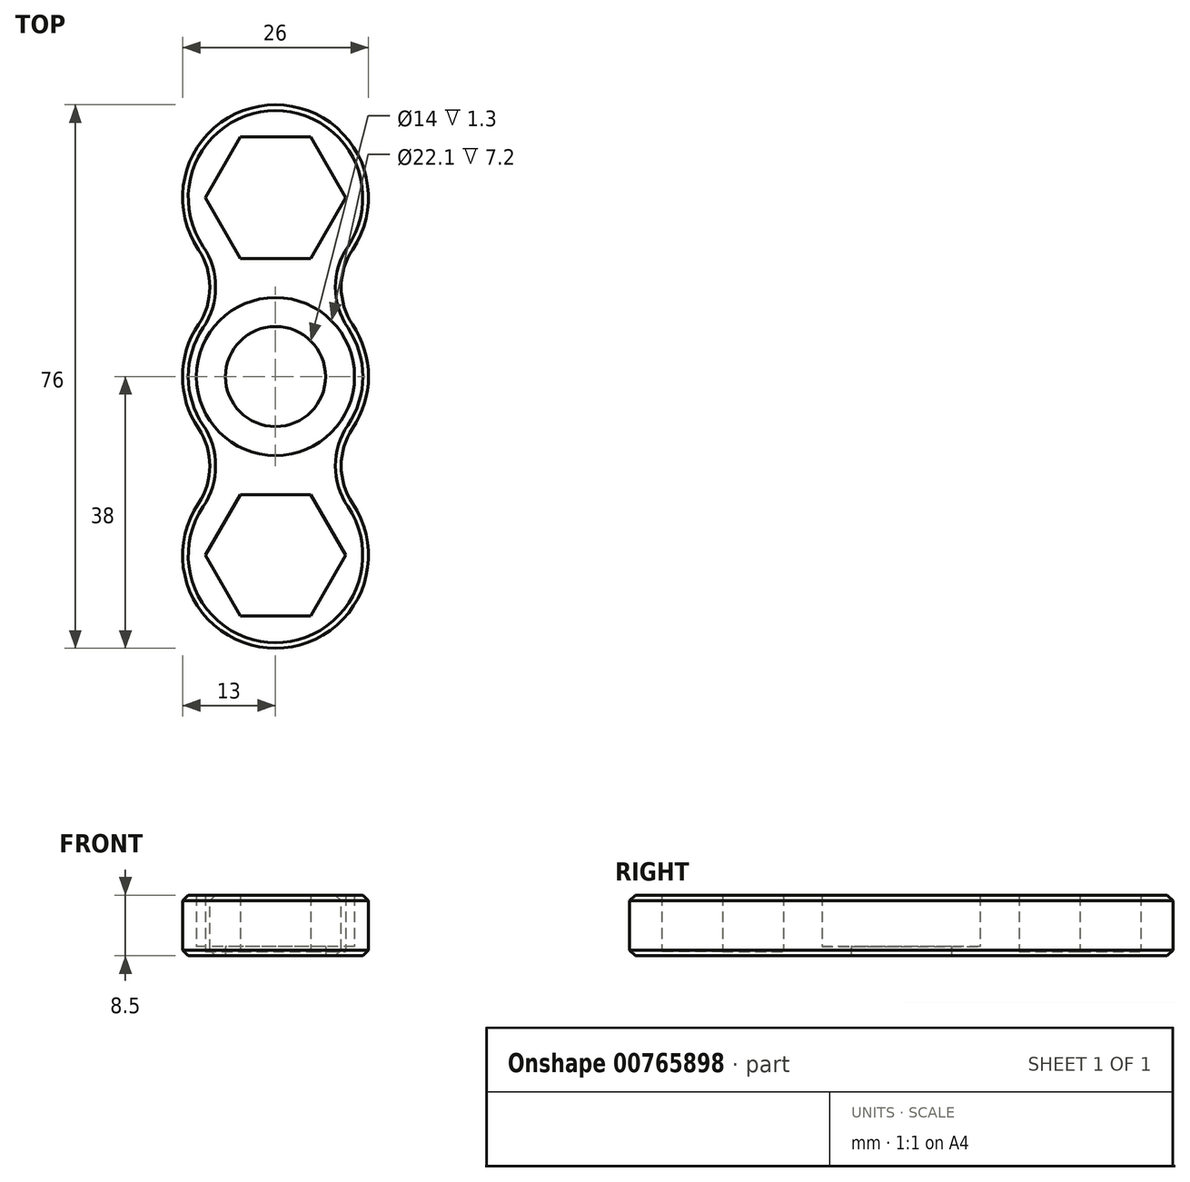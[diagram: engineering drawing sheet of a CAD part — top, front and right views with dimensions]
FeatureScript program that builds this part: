
annotation { "Feature Type Name" : "Feature", "Feature Type Description" : "" }
export const myFeature = defineFeature(function(context is Context, id is Id, definition is map)
    precondition{}
    {
        {
            var Q0;
            Q0=qCreatedBy(makeId("Top.planeOp"),FACE);
            var sketch = newSketch(context, id + "F0", { "sketchPlane" : qUnion([Q0])});
            skCircle(sketch, "E0", {"center": v(0, 0) * mm, "radius": 13 * mm});
            skCircle(sketch, "E1", {"center": v(0, 0) * mm, "radius": 11.05 * mm});
            skCircle(sketch, "E2", {"center": v(0, 25) * mm, "radius": 13 * mm});
            skCircle(sketch, "E3.cCircle", {"center": v(0, 25) * mm, "radius": 8.5 * mm, "construction": true});
            skLineSegment(sketch, "E3.0", {"start": v(9.81, 25) * mm, "end": v(4.9, 16.5) * mm});
            skLineSegment(sketch, "E3.1", {"start": v(4.9, 16.5) * mm, "end": v(-4.9, 16.5) * mm});
            skLineSegment(sketch, "E3.2", {"start": v(-4.9, 16.5) * mm, "end": v(-9.81, 25) * mm});
            skLineSegment(sketch, "E3.3", {"start": v(-9.81, 25) * mm, "end": v(-4.9, 33.5) * mm});
            skLineSegment(sketch, "E3.4", {"start": v(-4.9, 33.5) * mm, "end": v(4.9, 33.5) * mm});
            skLineSegment(sketch, "E3.5", {"start": v(4.9, 33.5) * mm, "end": v(9.81, 25) * mm});
            skPoint(sketch, "E3.0.midPoint", {"position": v(7.36, 20.75) * mm});
            skCircle(sketch, "E4.MirrorC", {"center": v(0, -25) * mm, "radius": 13 * mm});
            skLineSegment(sketch, "E5.MirrorCS", {"start": v(-4.9, -16.5) * mm, "end": v(-9.81, -25) * mm});
            skCircle(sketch, "E6.MirrorC", {"center": v(0, -25) * mm, "radius": 8.5 * mm, "construction": true});
            skLineSegment(sketch, "E7.MirrorCS", {"start": v(-9.81, -25) * mm, "end": v(-4.9, -33.5) * mm});
            skLineSegment(sketch, "E8.MirrorCS", {"start": v(-4.9, -33.5) * mm, "end": v(4.9, -33.5) * mm});
            skLineSegment(sketch, "E9.MirrorCS", {"start": v(4.9, -33.5) * mm, "end": v(9.81, -25) * mm});
            skLineSegment(sketch, "E10.MirrorCS", {"start": v(9.81, -25) * mm, "end": v(4.9, -16.5) * mm});
            skLineSegment(sketch, "E11.MirrorCS", {"start": v(4.9, -16.5) * mm, "end": v(-4.9, -16.5) * mm});
            skCircle(sketch, "E12", {"center": v(0, 0) * mm, "radius": 7 * mm});
            skSolve(sketch);
        }
        {
            var Q0;
            Q0=makeQuery(id+"F0.imprint","IMPRINT",FACE,{"disambiguationData":[TD([[makeQuery(id+"F0.imprint","IMPRINT",EDGE,{"derivedFrom":sQuery(id+"F0.wireOp",EDGE,"E3.0")}),1.0]])]});
            var Q1;
            Q1=makeQuery(id+"F0.imprint","IMPRINT",FACE,{"disambiguationData":[TD([[makeQuery(id+"F0.imprint","IMPRINT",EDGE,{"derivedFrom":sQuery(id+"F0.wireOp",EDGE,"E3.0")}),-1.0]])]});
            var Q2;
            Q2=makeQuery(id+"F0.imprint","IMPRINT",FACE,{"disambiguationData":[TD([[makeQuery(id+"F0.imprint","IMPRINT",EDGE,{"derivedFrom":sQuery(id+"F0.wireOp",EDGE,"E1")}),1.0]])]});
            var Q3;
            Q3=makeQuery(id+"F0.imprint","IMPRINT",FACE,{"disambiguationData":[TD([[makeQuery(id+"F0.imprint","IMPRINT",EDGE,{"derivedFrom":sQuery(id+"F0.wireOp",EDGE,"E1")}),-1.0]])]});
            var Q4;
            {var subQ0=sQuery(id+"F0.wireOp",EDGE,"E2");var subQ1=sQuery(id+"F0.wireOp",EDGE,"E0");var subQ2=makeQuery(id+"F0.imprint","INTERSECT",VERTEX,{"disambiguationData":[OD(0.0)],"derivedFrom":[subQ1,subQ0]});Q4=makeQuery(id+"F0.imprint","IMPRINT",FACE,{"disambiguationData":[TD([[makeQuery(id+"F0.imprint","IMPRINT",EDGE,{"disambiguationData":[TD([[subQ2,1.0]])],"derivedFrom":subQ1}),1.0]])]});}
            var Q5;
            {var subQ0=sQuery(id+"F0.wireOp",EDGE,"E4.MirrorC");var subQ1=sQuery(id+"F0.wireOp",EDGE,"E0");var subQ2=makeQuery(id+"F0.imprint","INTERSECT",VERTEX,{"disambiguationData":[OD(0.0)],"derivedFrom":[subQ1,subQ0]});Q5=makeQuery(id+"F0.imprint","IMPRINT",FACE,{"disambiguationData":[TD([[makeQuery(id+"F0.imprint","IMPRINT",EDGE,{"disambiguationData":[TD([[subQ2,-1.0]])],"derivedFrom":subQ1}),1.0]])]});}
            var Q6;
            Q6=makeQuery(id+"F0.imprint","IMPRINT",FACE,{"disambiguationData":[TD([[makeQuery(id+"F0.imprint","IMPRINT",EDGE,{"derivedFrom":sQuery(id+"F0.wireOp",EDGE,"E5.MirrorCS")}),-1.0]])]});
            var Q7;
            Q7=makeQuery(id+"F0.imprint","IMPRINT",FACE,{"disambiguationData":[TD([[makeQuery(id+"F0.imprint","IMPRINT",EDGE,{"derivedFrom":sQuery(id+"F0.wireOp",EDGE,"E5.MirrorCS")}),1.0]])]});
            extrude(context, id + "F1", {"entities" : qUnion([Q0, Q1, Q2, Q3, Q4, Q5, Q6, Q7]), "depth" : 0.6 * mm, "offsetDistance" : 25 * mm});
        }
        {
            var Q0;
            Q0=makeQuery(id+"F0.imprint","IMPRINT",FACE,{"disambiguationData":[TD([[makeQuery(id+"F0.imprint","IMPRINT",EDGE,{"derivedFrom":sQuery(id+"F0.wireOp",EDGE,"E3.0")}),1.0]])]});
            var Q1;
            Q1=makeQuery(id+"F0.imprint","IMPRINT",FACE,{"disambiguationData":[TD([[makeQuery(id+"F0.imprint","IMPRINT",EDGE,{"derivedFrom":sQuery(id+"F0.wireOp",EDGE,"E1")}),-1.0]])]});
            var Q2;
            {var subQ0=sQuery(id+"F0.wireOp",EDGE,"E2");var subQ1=sQuery(id+"F0.wireOp",EDGE,"E0");var subQ2=makeQuery(id+"F0.imprint","INTERSECT",VERTEX,{"disambiguationData":[OD(0.0)],"derivedFrom":[subQ1,subQ0]});Q2=makeQuery(id+"F0.imprint","IMPRINT",FACE,{"disambiguationData":[TD([[makeQuery(id+"F0.imprint","IMPRINT",EDGE,{"disambiguationData":[TD([[subQ2,1.0]])],"derivedFrom":subQ1}),1.0]])]});}
            var Q3;
            {var subQ0=sQuery(id+"F0.wireOp",EDGE,"E4.MirrorC");var subQ1=sQuery(id+"F0.wireOp",EDGE,"E0");var subQ2=makeQuery(id+"F0.imprint","INTERSECT",VERTEX,{"disambiguationData":[OD(0.0)],"derivedFrom":[subQ1,subQ0]});Q3=makeQuery(id+"F0.imprint","IMPRINT",FACE,{"disambiguationData":[TD([[makeQuery(id+"F0.imprint","IMPRINT",EDGE,{"disambiguationData":[TD([[subQ2,-1.0]])],"derivedFrom":subQ1}),1.0]])]});}
            var Q4;
            Q4=makeQuery(id+"F0.imprint","IMPRINT",FACE,{"disambiguationData":[TD([[makeQuery(id+"F0.imprint","IMPRINT",EDGE,{"derivedFrom":sQuery(id+"F0.wireOp",EDGE,"E5.MirrorCS")}),-1.0]])]});
            extrude(context, id + "F2", {"entities" : qUnion([Q0, Q1, Q2, Q3, Q4]), "operationType" : NewBodyOperationType.ADD, "depth" : 8.5 * mm, "offsetDistance" : 25 * mm});
        }
        {
            var Q0;
            {var subQ0=sQuery(id+"F0.wireOp",EDGE,"E4.MirrorC");var subQ1=sQuery(id+"F0.wireOp",EDGE,"E0");var subQ2=makeQuery(id+"F0.imprint","INTERSECT",VERTEX,{"disambiguationData":[OD(1.0)],"derivedFrom":[subQ1,subQ0]});Q0=makeQuery(id+"F2.boolean.opBoolean","MERGE",EDGE,{"derivedFrom":[makeQuery(id+"F1.opExtrude","SWEPT_EDGE",EDGE,{"disambiguationData":[OSD([subQ1,subQ0]),TDD([subQ2])]}),makeQuery(id+"F2.opExtrude","SWEPT_EDGE",EDGE,{"disambiguationData":[OSD([subQ1,subQ0]),TDD([subQ2])]})]});}
            var Q1;
            {var subQ0=sQuery(id+"F0.wireOp",EDGE,"E2");var subQ1=sQuery(id+"F0.wireOp",EDGE,"E0");var subQ2=makeQuery(id+"F0.imprint","INTERSECT",VERTEX,{"disambiguationData":[OD(1.0)],"derivedFrom":[subQ1,subQ0]});Q1=makeQuery(id+"F2.boolean.opBoolean","MERGE",EDGE,{"derivedFrom":[makeQuery(id+"F1.opExtrude","SWEPT_EDGE",EDGE,{"disambiguationData":[OSD([subQ1,subQ0]),TDD([subQ2])]}),makeQuery(id+"F2.opExtrude","SWEPT_EDGE",EDGE,{"disambiguationData":[OSD([subQ1,subQ0]),TDD([subQ2])]})]});}
            var Q2;
            {var subQ0=sQuery(id+"F0.wireOp",EDGE,"E2");var subQ1=sQuery(id+"F0.wireOp",EDGE,"E0");var subQ2=makeQuery(id+"F0.imprint","INTERSECT",VERTEX,{"disambiguationData":[OD(0.0)],"derivedFrom":[subQ1,subQ0]});Q2=makeQuery(id+"F2.boolean.opBoolean","MERGE",EDGE,{"derivedFrom":[makeQuery(id+"F1.opExtrude","SWEPT_EDGE",EDGE,{"disambiguationData":[OSD([subQ1,subQ0]),TDD([subQ2])]}),makeQuery(id+"F2.opExtrude","SWEPT_EDGE",EDGE,{"disambiguationData":[OSD([subQ1,subQ0]),TDD([subQ2])]})]});}
            var Q3;
            {var subQ0=sQuery(id+"F0.wireOp",EDGE,"E4.MirrorC");var subQ1=sQuery(id+"F0.wireOp",EDGE,"E0");var subQ2=makeQuery(id+"F0.imprint","INTERSECT",VERTEX,{"disambiguationData":[OD(0.0)],"derivedFrom":[subQ1,subQ0]});Q3=makeQuery(id+"F2.boolean.opBoolean","MERGE",EDGE,{"derivedFrom":[makeQuery(id+"F1.opExtrude","SWEPT_EDGE",EDGE,{"disambiguationData":[OSD([subQ1,subQ0]),TDD([subQ2])]}),makeQuery(id+"F2.opExtrude","SWEPT_EDGE",EDGE,{"disambiguationData":[OSD([subQ1,subQ0]),TDD([subQ2])]})]});}
            fillet(context, id + "F3", {"entities" : qUnion([Q0, Q1, Q2, Q3]), "radius" : 9.35 * mm, "tangentPropagation" : true, "allowEdgeOverflow" : false});
        }
        {
            var Q0;
            Q0=makeQuery(id+"F2.opExtrude","CAP_EDGE",EDGE,{"disambiguationData":[OSD([sQuery(id+"F0.wireOp",EDGE,"E4.MirrorC")])],"isStart":false});
            var Q1;
            {var subQ0=sQuery(id+"F0.wireOp",EDGE,"E4.MirrorC");var subQ1=sQuery(id+"F0.wireOp",EDGE,"E0");var subQ2=makeQuery(id+"F0.imprint","INTERSECT",VERTEX,{"disambiguationData":[OD(1.0)],"derivedFrom":[subQ1,subQ0]});Q1=makeQuery(id+"F3.opFillet","BLEND_EDGE",EDGE,{"blendedFrom":[makeQuery(id+"F2.boolean.opBoolean","MERGE",EDGE,{"derivedFrom":[makeQuery(id+"F1.opExtrude","SWEPT_EDGE",EDGE,{"disambiguationData":[OSD([subQ1,subQ0]),TDD([subQ2])]}),makeQuery(id+"F2.opExtrude","SWEPT_EDGE",EDGE,{"disambiguationData":[OSD([subQ1,subQ0]),TDD([subQ2])]})]}),makeQuery(id+"F2.opExtrude","CAP_FACE",FACE,{"disambiguationData":[OSD([subQ1,sQuery(id+"F0.wireOp",EDGE,"E1"),sQuery(id+"F0.wireOp",EDGE,"E2"),sQuery(id+"F0.wireOp",EDGE,"E3.0"),sQuery(id+"F0.wireOp",EDGE,"E3.1"),sQuery(id+"F0.wireOp",EDGE,"E3.2"),sQuery(id+"F0.wireOp",EDGE,"E3.3"),sQuery(id+"F0.wireOp",EDGE,"E3.4"),sQuery(id+"F0.wireOp",EDGE,"E3.5"),subQ0,sQuery(id+"F0.wireOp",EDGE,"E5.MirrorCS"),sQuery(id+"F0.wireOp",EDGE,"E7.MirrorCS"),sQuery(id+"F0.wireOp",EDGE,"E8.MirrorCS"),sQuery(id+"F0.wireOp",EDGE,"E9.MirrorCS"),sQuery(id+"F0.wireOp",EDGE,"E10.MirrorCS"),sQuery(id+"F0.wireOp",EDGE,"E11.MirrorCS")])],"isStart":false})],"blendedInto":[makeQuery(id+"F2.opExtrude","CAP_FACE",FACE,{"disambiguationData":[OSD([subQ1,sQuery(id+"F0.wireOp",EDGE,"E1"),sQuery(id+"F0.wireOp",EDGE,"E2"),sQuery(id+"F0.wireOp",EDGE,"E3.0"),sQuery(id+"F0.wireOp",EDGE,"E3.1"),sQuery(id+"F0.wireOp",EDGE,"E3.2"),sQuery(id+"F0.wireOp",EDGE,"E3.3"),sQuery(id+"F0.wireOp",EDGE,"E3.4"),sQuery(id+"F0.wireOp",EDGE,"E3.5"),subQ0,sQuery(id+"F0.wireOp",EDGE,"E5.MirrorCS"),sQuery(id+"F0.wireOp",EDGE,"E7.MirrorCS"),sQuery(id+"F0.wireOp",EDGE,"E8.MirrorCS"),sQuery(id+"F0.wireOp",EDGE,"E9.MirrorCS"),sQuery(id+"F0.wireOp",EDGE,"E10.MirrorCS"),sQuery(id+"F0.wireOp",EDGE,"E11.MirrorCS")])],"isStart":false})]});}
            var Q2;
            {var subQ0=sQuery(id+"F0.wireOp",EDGE,"E0");Q2=makeQuery(id+"F2.opExtrude","CAP_EDGE",EDGE,{"disambiguationData":[OSD([subQ0]),TDD([makeQuery(id+"F0.imprint","IMPRINT",EDGE,{"disambiguationData":[TD([[makeQuery(id+"F0.imprint","INTERSECT",VERTEX,{"disambiguationData":[OD(1.0)],"derivedFrom":[subQ0,sQuery(id+"F0.wireOp",EDGE,"E2")]}),1.0]])],"derivedFrom":subQ0})])],"isStart":false});}
            var Q3;
            {var subQ0=sQuery(id+"F0.wireOp",EDGE,"E2");var subQ1=sQuery(id+"F0.wireOp",EDGE,"E0");var subQ2=makeQuery(id+"F0.imprint","INTERSECT",VERTEX,{"disambiguationData":[OD(1.0)],"derivedFrom":[subQ1,subQ0]});Q3=makeQuery(id+"F3.opFillet","BLEND_EDGE",EDGE,{"blendedFrom":[makeQuery(id+"F2.boolean.opBoolean","MERGE",EDGE,{"derivedFrom":[makeQuery(id+"F1.opExtrude","SWEPT_EDGE",EDGE,{"disambiguationData":[OSD([subQ1,subQ0]),TDD([subQ2])]}),makeQuery(id+"F2.opExtrude","SWEPT_EDGE",EDGE,{"disambiguationData":[OSD([subQ1,subQ0]),TDD([subQ2])]})]}),makeQuery(id+"F2.opExtrude","CAP_FACE",FACE,{"disambiguationData":[OSD([subQ1,sQuery(id+"F0.wireOp",EDGE,"E1"),subQ0,sQuery(id+"F0.wireOp",EDGE,"E3.0"),sQuery(id+"F0.wireOp",EDGE,"E3.1"),sQuery(id+"F0.wireOp",EDGE,"E3.2"),sQuery(id+"F0.wireOp",EDGE,"E3.3"),sQuery(id+"F0.wireOp",EDGE,"E3.4"),sQuery(id+"F0.wireOp",EDGE,"E3.5"),sQuery(id+"F0.wireOp",EDGE,"E4.MirrorC"),sQuery(id+"F0.wireOp",EDGE,"E5.MirrorCS"),sQuery(id+"F0.wireOp",EDGE,"E7.MirrorCS"),sQuery(id+"F0.wireOp",EDGE,"E8.MirrorCS"),sQuery(id+"F0.wireOp",EDGE,"E9.MirrorCS"),sQuery(id+"F0.wireOp",EDGE,"E10.MirrorCS"),sQuery(id+"F0.wireOp",EDGE,"E11.MirrorCS")])],"isStart":false})],"blendedInto":[makeQuery(id+"F2.opExtrude","CAP_FACE",FACE,{"disambiguationData":[OSD([subQ1,sQuery(id+"F0.wireOp",EDGE,"E1"),subQ0,sQuery(id+"F0.wireOp",EDGE,"E3.0"),sQuery(id+"F0.wireOp",EDGE,"E3.1"),sQuery(id+"F0.wireOp",EDGE,"E3.2"),sQuery(id+"F0.wireOp",EDGE,"E3.3"),sQuery(id+"F0.wireOp",EDGE,"E3.4"),sQuery(id+"F0.wireOp",EDGE,"E3.5"),sQuery(id+"F0.wireOp",EDGE,"E4.MirrorC"),sQuery(id+"F0.wireOp",EDGE,"E5.MirrorCS"),sQuery(id+"F0.wireOp",EDGE,"E7.MirrorCS"),sQuery(id+"F0.wireOp",EDGE,"E8.MirrorCS"),sQuery(id+"F0.wireOp",EDGE,"E9.MirrorCS"),sQuery(id+"F0.wireOp",EDGE,"E10.MirrorCS"),sQuery(id+"F0.wireOp",EDGE,"E11.MirrorCS")])],"isStart":false})]});}
            var Q4;
            Q4=makeQuery(id+"F2.opExtrude","CAP_EDGE",EDGE,{"disambiguationData":[OSD([sQuery(id+"F0.wireOp",EDGE,"E2")])],"isStart":false});
            var Q5;
            {var subQ0=sQuery(id+"F0.wireOp",EDGE,"E2");var subQ1=sQuery(id+"F0.wireOp",EDGE,"E0");var subQ2=makeQuery(id+"F0.imprint","INTERSECT",VERTEX,{"disambiguationData":[OD(0.0)],"derivedFrom":[subQ1,subQ0]});Q5=makeQuery(id+"F3.opFillet","BLEND_EDGE",EDGE,{"blendedFrom":[makeQuery(id+"F2.boolean.opBoolean","MERGE",EDGE,{"derivedFrom":[makeQuery(id+"F1.opExtrude","SWEPT_EDGE",EDGE,{"disambiguationData":[OSD([subQ1,subQ0]),TDD([subQ2])]}),makeQuery(id+"F2.opExtrude","SWEPT_EDGE",EDGE,{"disambiguationData":[OSD([subQ1,subQ0]),TDD([subQ2])]})]}),makeQuery(id+"F2.opExtrude","CAP_FACE",FACE,{"disambiguationData":[OSD([subQ1,sQuery(id+"F0.wireOp",EDGE,"E1"),subQ0,sQuery(id+"F0.wireOp",EDGE,"E3.0"),sQuery(id+"F0.wireOp",EDGE,"E3.1"),sQuery(id+"F0.wireOp",EDGE,"E3.2"),sQuery(id+"F0.wireOp",EDGE,"E3.3"),sQuery(id+"F0.wireOp",EDGE,"E3.4"),sQuery(id+"F0.wireOp",EDGE,"E3.5"),sQuery(id+"F0.wireOp",EDGE,"E4.MirrorC"),sQuery(id+"F0.wireOp",EDGE,"E5.MirrorCS"),sQuery(id+"F0.wireOp",EDGE,"E7.MirrorCS"),sQuery(id+"F0.wireOp",EDGE,"E8.MirrorCS"),sQuery(id+"F0.wireOp",EDGE,"E9.MirrorCS"),sQuery(id+"F0.wireOp",EDGE,"E10.MirrorCS"),sQuery(id+"F0.wireOp",EDGE,"E11.MirrorCS")])],"isStart":false})],"blendedInto":[makeQuery(id+"F2.opExtrude","CAP_FACE",FACE,{"disambiguationData":[OSD([subQ1,sQuery(id+"F0.wireOp",EDGE,"E1"),subQ0,sQuery(id+"F0.wireOp",EDGE,"E3.0"),sQuery(id+"F0.wireOp",EDGE,"E3.1"),sQuery(id+"F0.wireOp",EDGE,"E3.2"),sQuery(id+"F0.wireOp",EDGE,"E3.3"),sQuery(id+"F0.wireOp",EDGE,"E3.4"),sQuery(id+"F0.wireOp",EDGE,"E3.5"),sQuery(id+"F0.wireOp",EDGE,"E4.MirrorC"),sQuery(id+"F0.wireOp",EDGE,"E5.MirrorCS"),sQuery(id+"F0.wireOp",EDGE,"E7.MirrorCS"),sQuery(id+"F0.wireOp",EDGE,"E8.MirrorCS"),sQuery(id+"F0.wireOp",EDGE,"E9.MirrorCS"),sQuery(id+"F0.wireOp",EDGE,"E10.MirrorCS"),sQuery(id+"F0.wireOp",EDGE,"E11.MirrorCS")])],"isStart":false})]});}
            var Q6;
            {var subQ0=sQuery(id+"F0.wireOp",EDGE,"E0");Q6=makeQuery(id+"F2.opExtrude","CAP_EDGE",EDGE,{"disambiguationData":[OSD([subQ0]),TDD([makeQuery(id+"F0.imprint","IMPRINT",EDGE,{"disambiguationData":[TD([[makeQuery(id+"F0.imprint","INTERSECT",VERTEX,{"disambiguationData":[OD(0.0)],"derivedFrom":[subQ0,sQuery(id+"F0.wireOp",EDGE,"E2")]}),-1.0]])],"derivedFrom":subQ0})])],"isStart":false});}
            var Q7;
            {var subQ0=sQuery(id+"F0.wireOp",EDGE,"E4.MirrorC");var subQ1=sQuery(id+"F0.wireOp",EDGE,"E0");var subQ2=makeQuery(id+"F0.imprint","INTERSECT",VERTEX,{"disambiguationData":[OD(0.0)],"derivedFrom":[subQ1,subQ0]});Q7=makeQuery(id+"F3.opFillet","BLEND_EDGE",EDGE,{"blendedFrom":[makeQuery(id+"F2.boolean.opBoolean","MERGE",EDGE,{"derivedFrom":[makeQuery(id+"F1.opExtrude","SWEPT_EDGE",EDGE,{"disambiguationData":[OSD([subQ1,subQ0]),TDD([subQ2])]}),makeQuery(id+"F2.opExtrude","SWEPT_EDGE",EDGE,{"disambiguationData":[OSD([subQ1,subQ0]),TDD([subQ2])]})]}),makeQuery(id+"F2.opExtrude","CAP_FACE",FACE,{"disambiguationData":[OSD([subQ1,sQuery(id+"F0.wireOp",EDGE,"E1"),sQuery(id+"F0.wireOp",EDGE,"E2"),sQuery(id+"F0.wireOp",EDGE,"E3.0"),sQuery(id+"F0.wireOp",EDGE,"E3.1"),sQuery(id+"F0.wireOp",EDGE,"E3.2"),sQuery(id+"F0.wireOp",EDGE,"E3.3"),sQuery(id+"F0.wireOp",EDGE,"E3.4"),sQuery(id+"F0.wireOp",EDGE,"E3.5"),subQ0,sQuery(id+"F0.wireOp",EDGE,"E5.MirrorCS"),sQuery(id+"F0.wireOp",EDGE,"E7.MirrorCS"),sQuery(id+"F0.wireOp",EDGE,"E8.MirrorCS"),sQuery(id+"F0.wireOp",EDGE,"E9.MirrorCS"),sQuery(id+"F0.wireOp",EDGE,"E10.MirrorCS"),sQuery(id+"F0.wireOp",EDGE,"E11.MirrorCS")])],"isStart":false})],"blendedInto":[makeQuery(id+"F2.opExtrude","CAP_FACE",FACE,{"disambiguationData":[OSD([subQ1,sQuery(id+"F0.wireOp",EDGE,"E1"),sQuery(id+"F0.wireOp",EDGE,"E2"),sQuery(id+"F0.wireOp",EDGE,"E3.0"),sQuery(id+"F0.wireOp",EDGE,"E3.1"),sQuery(id+"F0.wireOp",EDGE,"E3.2"),sQuery(id+"F0.wireOp",EDGE,"E3.3"),sQuery(id+"F0.wireOp",EDGE,"E3.4"),sQuery(id+"F0.wireOp",EDGE,"E3.5"),subQ0,sQuery(id+"F0.wireOp",EDGE,"E5.MirrorCS"),sQuery(id+"F0.wireOp",EDGE,"E7.MirrorCS"),sQuery(id+"F0.wireOp",EDGE,"E8.MirrorCS"),sQuery(id+"F0.wireOp",EDGE,"E9.MirrorCS"),sQuery(id+"F0.wireOp",EDGE,"E10.MirrorCS"),sQuery(id+"F0.wireOp",EDGE,"E11.MirrorCS")])],"isStart":false})]});}
            var Q8;
            Q8=makeQuery(id+"F1.opExtrude","CAP_EDGE",EDGE,{"disambiguationData":[OSD([sQuery(id+"F0.wireOp",EDGE,"E4.MirrorC")])],"isStart":true});
            var Q9;
            {var subQ0=sQuery(id+"F0.wireOp",EDGE,"E4.MirrorC");var subQ1=sQuery(id+"F0.wireOp",EDGE,"E0");var subQ2=makeQuery(id+"F0.imprint","INTERSECT",VERTEX,{"disambiguationData":[OD(0.0)],"derivedFrom":[subQ1,subQ0]});Q9=makeQuery(id+"F3.opFillet","BLEND_EDGE",EDGE,{"blendedFrom":[makeQuery(id+"F2.boolean.opBoolean","MERGE",EDGE,{"derivedFrom":[makeQuery(id+"F1.opExtrude","SWEPT_EDGE",EDGE,{"disambiguationData":[OSD([subQ1,subQ0]),TDD([subQ2])]}),makeQuery(id+"F2.opExtrude","SWEPT_EDGE",EDGE,{"disambiguationData":[OSD([subQ1,subQ0]),TDD([subQ2])]})]}),makeQuery(id+"F1.opExtrude","CAP_FACE",FACE,{"disambiguationData":[OSD([subQ1,sQuery(id+"F0.wireOp",EDGE,"E2"),subQ0,sQuery(id+"F0.wireOp",EDGE,"E12")])],"isStart":true})],"blendedInto":[makeQuery(id+"F1.opExtrude","CAP_FACE",FACE,{"disambiguationData":[OSD([subQ1,sQuery(id+"F0.wireOp",EDGE,"E2"),subQ0,sQuery(id+"F0.wireOp",EDGE,"E12")])],"isStart":true})]});}
            var Q10;
            {var subQ0=sQuery(id+"F0.wireOp",EDGE,"E0");Q10=makeQuery(id+"F1.opExtrude","CAP_EDGE",EDGE,{"disambiguationData":[OSD([subQ0]),TDD([makeQuery(id+"F0.imprint","IMPRINT",EDGE,{"disambiguationData":[TD([[makeQuery(id+"F0.imprint","INTERSECT",VERTEX,{"disambiguationData":[OD(0.0)],"derivedFrom":[subQ0,sQuery(id+"F0.wireOp",EDGE,"E2")]}),-1.0]])],"derivedFrom":subQ0})])],"isStart":true});}
            var Q11;
            {var subQ0=sQuery(id+"F0.wireOp",EDGE,"E2");var subQ1=sQuery(id+"F0.wireOp",EDGE,"E0");var subQ2=makeQuery(id+"F0.imprint","INTERSECT",VERTEX,{"disambiguationData":[OD(0.0)],"derivedFrom":[subQ1,subQ0]});Q11=makeQuery(id+"F3.opFillet","BLEND_EDGE",EDGE,{"blendedFrom":[makeQuery(id+"F2.boolean.opBoolean","MERGE",EDGE,{"derivedFrom":[makeQuery(id+"F1.opExtrude","SWEPT_EDGE",EDGE,{"disambiguationData":[OSD([subQ1,subQ0]),TDD([subQ2])]}),makeQuery(id+"F2.opExtrude","SWEPT_EDGE",EDGE,{"disambiguationData":[OSD([subQ1,subQ0]),TDD([subQ2])]})]}),makeQuery(id+"F1.opExtrude","CAP_FACE",FACE,{"disambiguationData":[OSD([subQ1,subQ0,sQuery(id+"F0.wireOp",EDGE,"E4.MirrorC"),sQuery(id+"F0.wireOp",EDGE,"E12")])],"isStart":true})],"blendedInto":[makeQuery(id+"F1.opExtrude","CAP_FACE",FACE,{"disambiguationData":[OSD([subQ1,subQ0,sQuery(id+"F0.wireOp",EDGE,"E4.MirrorC"),sQuery(id+"F0.wireOp",EDGE,"E12")])],"isStart":true})]});}
            var Q12;
            Q12=makeQuery(id+"F1.opExtrude","CAP_EDGE",EDGE,{"disambiguationData":[OSD([sQuery(id+"F0.wireOp",EDGE,"E2")])],"isStart":true});
            var Q13;
            {var subQ0=sQuery(id+"F0.wireOp",EDGE,"E2");var subQ1=sQuery(id+"F0.wireOp",EDGE,"E0");var subQ2=makeQuery(id+"F0.imprint","INTERSECT",VERTEX,{"disambiguationData":[OD(1.0)],"derivedFrom":[subQ1,subQ0]});Q13=makeQuery(id+"F3.opFillet","BLEND_EDGE",EDGE,{"blendedFrom":[makeQuery(id+"F2.boolean.opBoolean","MERGE",EDGE,{"derivedFrom":[makeQuery(id+"F1.opExtrude","SWEPT_EDGE",EDGE,{"disambiguationData":[OSD([subQ1,subQ0]),TDD([subQ2])]}),makeQuery(id+"F2.opExtrude","SWEPT_EDGE",EDGE,{"disambiguationData":[OSD([subQ1,subQ0]),TDD([subQ2])]})]}),makeQuery(id+"F1.opExtrude","CAP_FACE",FACE,{"disambiguationData":[OSD([subQ1,subQ0,sQuery(id+"F0.wireOp",EDGE,"E4.MirrorC"),sQuery(id+"F0.wireOp",EDGE,"E12")])],"isStart":true})],"blendedInto":[makeQuery(id+"F1.opExtrude","CAP_FACE",FACE,{"disambiguationData":[OSD([subQ1,subQ0,sQuery(id+"F0.wireOp",EDGE,"E4.MirrorC"),sQuery(id+"F0.wireOp",EDGE,"E12")])],"isStart":true})]});}
            var Q14;
            {var subQ0=sQuery(id+"F0.wireOp",EDGE,"E0");Q14=makeQuery(id+"F1.opExtrude","CAP_EDGE",EDGE,{"disambiguationData":[OSD([subQ0]),TDD([makeQuery(id+"F0.imprint","IMPRINT",EDGE,{"disambiguationData":[TD([[makeQuery(id+"F0.imprint","INTERSECT",VERTEX,{"disambiguationData":[OD(1.0)],"derivedFrom":[subQ0,sQuery(id+"F0.wireOp",EDGE,"E2")]}),1.0]])],"derivedFrom":subQ0})])],"isStart":true});}
            var Q15;
            {var subQ0=sQuery(id+"F0.wireOp",EDGE,"E4.MirrorC");var subQ1=sQuery(id+"F0.wireOp",EDGE,"E0");var subQ2=makeQuery(id+"F0.imprint","INTERSECT",VERTEX,{"disambiguationData":[OD(1.0)],"derivedFrom":[subQ1,subQ0]});Q15=makeQuery(id+"F3.opFillet","BLEND_EDGE",EDGE,{"blendedFrom":[makeQuery(id+"F2.boolean.opBoolean","MERGE",EDGE,{"derivedFrom":[makeQuery(id+"F1.opExtrude","SWEPT_EDGE",EDGE,{"disambiguationData":[OSD([subQ1,subQ0]),TDD([subQ2])]}),makeQuery(id+"F2.opExtrude","SWEPT_EDGE",EDGE,{"disambiguationData":[OSD([subQ1,subQ0]),TDD([subQ2])]})]}),makeQuery(id+"F1.opExtrude","CAP_FACE",FACE,{"disambiguationData":[OSD([subQ1,sQuery(id+"F0.wireOp",EDGE,"E2"),subQ0,sQuery(id+"F0.wireOp",EDGE,"E12")])],"isStart":true})],"blendedInto":[makeQuery(id+"F1.opExtrude","CAP_FACE",FACE,{"disambiguationData":[OSD([subQ1,sQuery(id+"F0.wireOp",EDGE,"E2"),subQ0,sQuery(id+"F0.wireOp",EDGE,"E12")])],"isStart":true})]});}
            chamfer(context, id + "F4", {"entities" : qUnion([Q0, Q1, Q2, Q3, Q4, Q5, Q6, Q7, Q8, Q9, Q10, Q11, Q12, Q13, Q14, Q15]), "width" : 0.8 * mm, "tangentPropagation" : true});
        }
        {
            var Q0;
            Q0=makeQuery(id+"F0.imprint","IMPRINT",FACE,{"disambiguationData":[TD([[makeQuery(id+"F0.imprint","IMPRINT",EDGE,{"derivedFrom":sQuery(id+"F0.wireOp",EDGE,"E1")}),1.0]])]});
            extrude(context, id + "F5", {"entities" : qUnion([Q0]), "operationType" : NewBodyOperationType.ADD, "depth" : 1.3 * mm, "offsetDistance" : 25 * mm});
        }
    });
